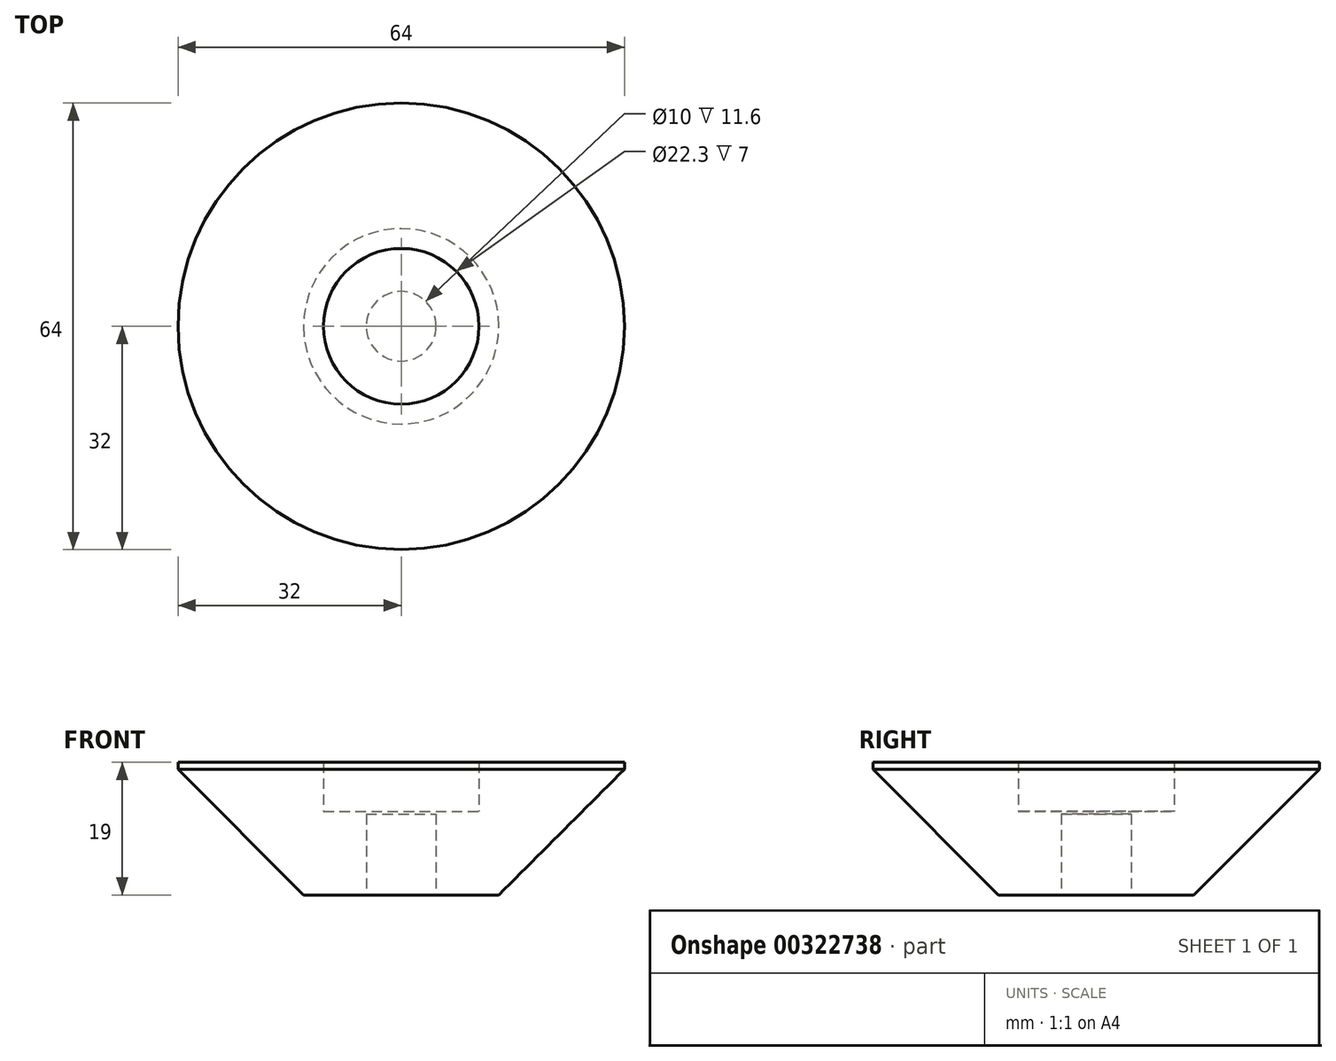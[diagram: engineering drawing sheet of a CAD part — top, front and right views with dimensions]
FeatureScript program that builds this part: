
annotation { "Feature Type Name" : "Feature", "Feature Type Description" : "" }
export const myFeature = defineFeature(function(context is Context, id is Id, definition is map)
    precondition{}
    {
        {
            var Q0;
            Q0=qCreatedBy(makeId("Front.planeOp"),FACE);
            var sketch = newSketch(context, id + "F0", { "sketchPlane" : qUnion([Q0])});
            skLineSegment(sketch, "E0", {"start": v(0, 0) * mm, "end": v(-14, 0) * mm});
            skLineSegment(sketch, "E1", {"start": v(-14, 0) * mm, "end": v(-33, 19) * mm});
            skLineSegment(sketch, "E2", {"start": v(-33, 19) * mm, "end": v(-11.15, 19) * mm});
            skLineSegment(sketch, "E3", {"start": v(-11.15, 19) * mm, "end": v(-11.15, 12) * mm});
            skLineSegment(sketch, "E4", {"start": v(-11.15, 12) * mm, "end": v(0, 12) * mm});
            skLineSegment(sketch, "E5", {"start": v(-5, 12) * mm, "end": v(-5, 0) * mm});
            skLineSegment(sketch, "E6", {"start": v(-5, 11.6) * mm, "end": v(0, 11.6) * mm});
            skLineSegment(sketch, "E7", {"start": v(0, 11.6) * mm, "end": v(0, 12) * mm});
            skSolve(sketch);
        }
        {
            var Q0;
            {var subQ1=sQuery(id+"F0.wireOp",EDGE,"E1");Q0=makeQuery(id+"F0.imprint","IMPRINT",FACE,{"disambiguationData":[TD([[makeQuery(id+"F0.imprint","IMPRINT",EDGE,{"derivedFrom":subQ1}),-1.0]])]});}
            var Q1;
            {var subQ4=sQuery(id+"F0.wireOp",EDGE,"E6");Q1=makeQuery(id+"F0.imprint","IMPRINT",FACE,{"disambiguationData":[TD([[makeQuery(id+"F0.imprint","IMPRINT",EDGE,{"derivedFrom":subQ4}),1.0]])]});}
            var Q2;
            Q2=sQuery(id+"F0.wireOp",EDGE,"E7");
            revolve(context, id + "F1", {"entities" : qUnion([Q0, Q1]), "axis" : qUnion([Q2]), "revolveType" : RevolveType.FULL});
        }
        {
            var Q0;
            Q0=qCreatedBy(makeId("Top.planeOp"),FACE);
            var sketch = newSketch(context, id + "F2", { "sketchPlane" : qUnion([Q0])});
            skCircle(sketch, "E8", {"center": v(0, 0) * mm, "radius": 32 * mm});
            skSolve(sketch);
        }
        {
            var Q0;
            Q0=makeQuery(id+"F2.imprint","IMPRINT",FACE,{"disambiguationData":[TD([[makeQuery(id+"F2.imprint","IMPRINT",EDGE,{"derivedFrom":sQuery(id+"F2.wireOp",EDGE,"E8")}),1.0]])]});
            extrude(context, id + "F3", {"entities" : qUnion([Q0]), "depth" : 25 * mm});
        }
        {
            var Q0;
            Q0=makeQuery(id+"F1.opRevolve","SWEPT_BODY",BODY,{"disambiguationData":[OSD([sQuery(id+"F0.wireOp",EDGE,"E0"),sQuery(id+"F0.wireOp",EDGE,"E1"),sQuery(id+"F0.wireOp",EDGE,"E2"),sQuery(id+"F0.wireOp",EDGE,"E3"),sQuery(id+"F0.wireOp",EDGE,"E4"),sQuery(id+"F0.wireOp",EDGE,"E5"),sQuery(id+"F0.wireOp",EDGE,"E6"),sQuery(id+"F0.wireOp",EDGE,"E7")])]});
            var Q1;
            Q1=makeQuery(id+"F3.opExtrude","SWEPT_BODY",BODY,{"disambiguationData":[OSD([sQuery(id+"F2.wireOp",EDGE,"E8")])]});
            booleanBodies(context, id + "F4", {"operationType" : BooleanOperationType.INTERSECTION, "tools" : qUnion([Q0, Q1])});
        }
    });
